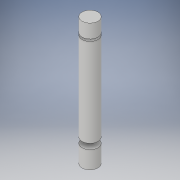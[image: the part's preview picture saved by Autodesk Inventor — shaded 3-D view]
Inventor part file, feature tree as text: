
AUTODESK INVENTOR PART (.ipt)
format: ipt  version: 2017 (Build 210142000, 142)  size: 122,368 bytes
history: native  units: in
note: dims shown in document units (in); Inventor stores cm internally (conversion verified against a paired STEP export)
features: extrude x2, sketch x2, projected_geometry x1
ambient origin geometry x8: Origin, YZ Plane, XZ Plane, XY Plane, X Axis, Y Axis, Z Axis, Center Point
bodies: Body1 (feature_tree)
feature tree (5):
  extrude  "Extrusion2"  Depth=2.25in
  extrude  "Extrusion3"  Depth=1.955in
  sketch  "Sketch2"  dims[d3=18.0in d4=2.25in]
  sketch  "Sketch3"  dims[d5=0.295in d6=1.955in d7=0.775in d8=2.475in d9=2.25in d10=0.0in d11=2.25in d12=1.125in d13=1.125in d14=18.0in d15=0.0in]
  projected_geometry  "Projected Loop1"
